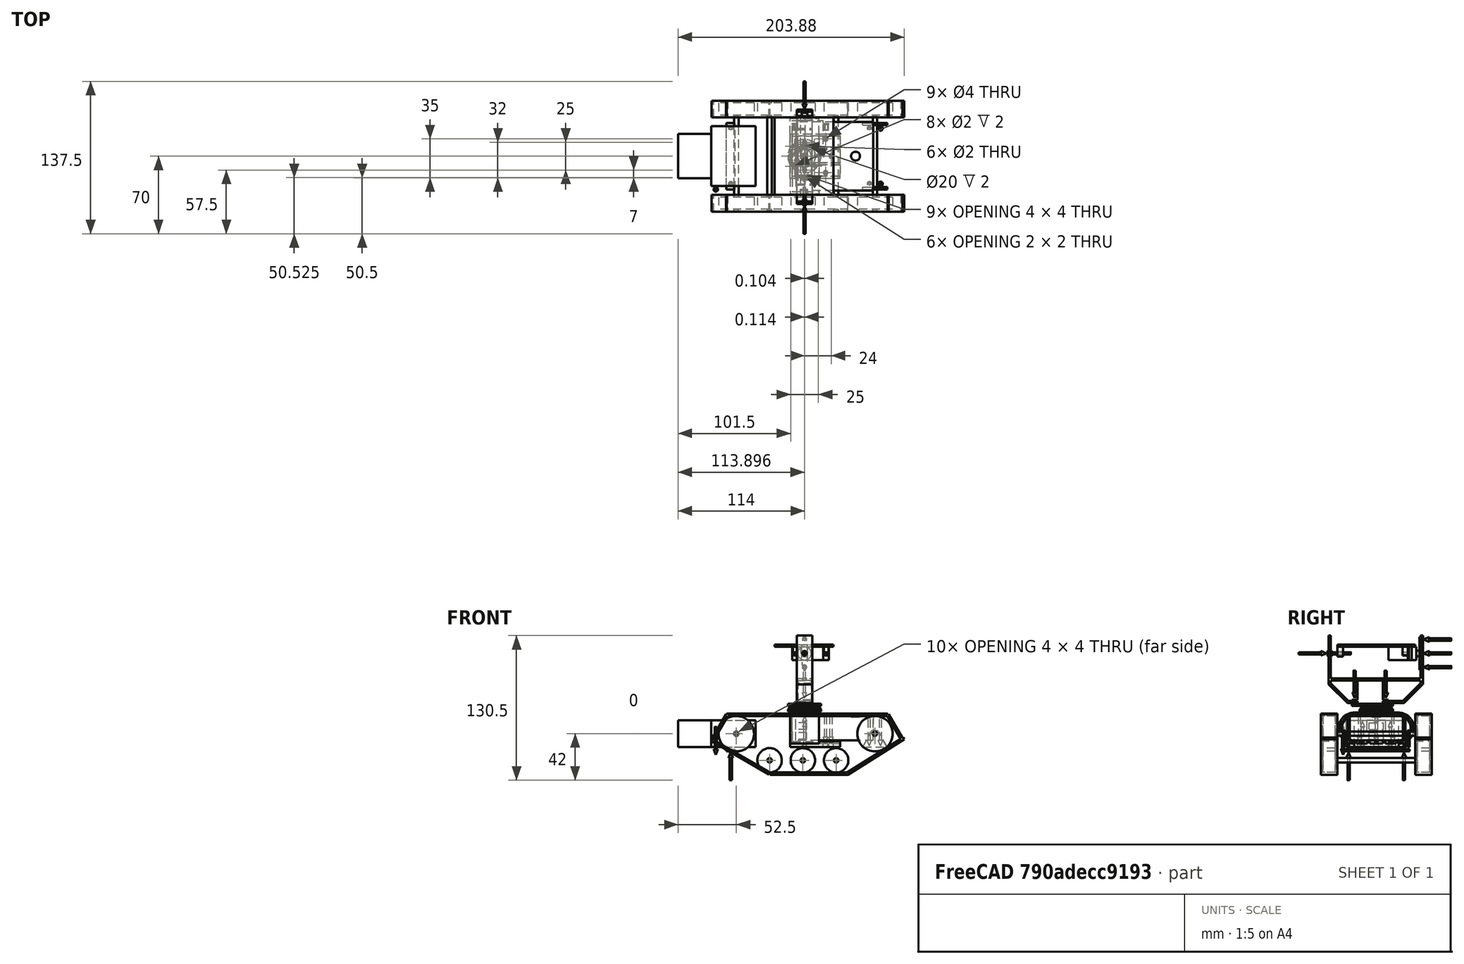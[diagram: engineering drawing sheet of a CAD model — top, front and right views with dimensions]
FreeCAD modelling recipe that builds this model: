
FCSTD DOCUMENT
Label: androidtank_10
License: CC-BY 3.0
LicenseURL: http://creativecommons.org/licenses/by/3.0/
objects: Part::Cylinder×59, Part::MultiFuse×47, Part::Box×40, Part::Cut×9, Part::Sphere×8, App::DocumentObjectGroup×3, Part::FeaturePython×1, Mesh::Feature×1, Part::Cone×1
note: 165 computed .brp shape members not serialized (recipe doc carries the construction recipe); baked Part::Feature solids carry a one-line shape summary decoded from their .brp

FEATURE [Part::Box] Box001001  label="Moter Unit2"
  Height = 24
  Length = 30
  Placement = pos=(-34,10,2) rot=(0,0,1;0rad)
  Width = 40
FEATURE [Part::Cylinder] Cylinder  label="Shaft"
  Angle = 360
  Height = 100
  Placement = pos=(20,-20,14) rot=(-1,0,0;1.5708rad)
  Radius = 2
FEATURE [Part::Box] Box001002
  Height = 2
  Length = 145
  Placement = pos=(10,-20,30) rot=(0,0,1;0rad)
  Width = 15
FEATURE [Part::Box] Box001002001
  Height = 2
  Length = 70
  Placement = pos=(49,-20,-23) rot=(0,0,1;0rad)
  Width = 15
FEATURE [Part::Box] Box001002001001
  Height = 2
  Length = 60
  Placement = pos=(119,-20,-23) rot=(0,-1,0;0.558505rad)
  Width = 15
FEATURE [Part::Box] Box001002001002
  Height = 2
  Length = 60
  Placement = pos=(49,-20,-21) rot=(0,1,0;3.66519rad)
  Width = 15
FEATURE [Part::Box] Box001002001003
  Height = 2
  Length = 26
  Placement = pos=(-2,-20,8) rot=(0,-1,0;1.0472rad)
  Width = 15
FEATURE [Part::Box] Box001002001003001
  Height = 2
  Length = 26
  Placement = pos=(169,-20,9) rot=(0,-1,0;2.0944rad)
  Width = 15
FEATURE [Part::MultiFuse] Fusion002001002  label="Caterpiller1"
  Shapes = -> [Box001002,Box001002001,Box001002001002,Box001002001001,Box001002001003,Box001002001003001]
FEATURE [Part::MultiFuse] Fusion002001002001  label="Caterpiller2"
  Placement = pos=(0,85,0) rot=(0,0,1;0rad)
  Shapes = -> [Box001002,Box001002001,Box001002001002,Box001002001001,Box001002001003,Box001002001003001]
FEATURE [Part::Cylinder] Cylinder002001001002  label="Wheel006"
  Angle = 360
  Height = 11
  Placement = pos=(20,78,14) rot=(1,0,0;1.5708rad)
  Radius = 11
FEATURE [Part::Cylinder] Cylinder002001001002001  label="Wheel007"
  Angle = 360
  Height = 11
  Placement = pos=(20,-7,14) rot=(1,0,0;1.5708rad)
  Radius = 11
FEATURE [Part::Cylinder] Cylinder002001002001  label="Shaft002"
  Angle = 360
  Height = 100
  Placement = pos=(20,-20,14) rot=(-1,0,0;1.5708rad)
  Radius = 2
FEATURE [Part::MultiFuse] Fusion002001002002002  label="SWheelSet1"
  Placement = pos=(28.5,0,-24) rot=(0,0,1;0rad)
  Shapes = -> [Cylinder002001002001,Cylinder002001001002,Cylinder002001001002001]
FEATURE [Part::MultiFuse] Fusion002001002002002001  label="SWheelSet2"
  Placement = pos=(58.5,0,-24) rot=(0,0,1;0rad)
  Shapes = -> [Cylinder002001002001,Cylinder002001001002,Cylinder002001001002001]
FEATURE [Part::MultiFuse] Fusion002001002002002001001  label="SWheelSet3"
  Placement = pos=(88.5,0,-24) rot=(0,0,1;0rad)
  Shapes = -> [Cylinder002001002001,Cylinder002001001002,Cylinder002001001002001]
FEATURE [Part::Box] Box001002001003002
  Height = 22
  Length = 70
  Placement = pos=(0,0,-11) rot=(0,0,1;0rad)
  Width = 40
FEATURE [Part::Cylinder] Cylinder002001001002002
  Angle = 360
  Height = 70
  Placement = pos=(0,0,0) rot=(0,1,0;1.5708rad)
  Radius = 11
FEATURE [Part::Cylinder] Cylinder001
  Angle = 360
  Height = 70
  Placement = pos=(0,40,0) rot=(0,1,0;1.5708rad)
  Radius = 11
FEATURE [Part::Cylinder] Cylinder002001001002003  label="PowerButton"
  Angle = 360
  Height = 2
  Placement = pos=(16,20,10) rot=(0,0,1;0rad)
  Radius = 4
FEATURE [Part::Box] Box001002001003003  label="USB1"
  Height = 6
  Length = 15
  Placement = pos=(60,13.5,-1) rot=(0,0,1;0rad)
  Width = 13
FEATURE [Part::Box] Box001001001  label="USB2"
  Height = 6
  Length = 15
  Placement = pos=(60,13.5,-10) rot=(0,0,1;0rad)
  Width = 13
FEATURE [Part::MultiFuse] Fusion002001002002002001002
  Shapes = -> [Cylinder001,Box001002001003002,Cylinder002001001002002]
FEATURE [Part::MultiFuse] Fusion001001
  Shapes = -> [Box001001001,Cylinder002001001002003,Box001002001003003]
FEATURE [Part::Cut] Cut  label="Eneloop"
  Base = -> Fusion002001002002002001002
  Placement = pos=(142,50,19) rot=(0,0,1;3.14159rad)
  Tool = -> Fusion001001
FEATURE [Part::Cylinder] Cylinder001001  label="Cylinder002"
  Angle = 360
  Height = 26
  Placement = pos=(0,50,19) rot=(0,1,0;1.5708rad)
  Radius = 14
FEATURE [Part::Box] Box001002001003002001  label="Box001002001003002001001001001006001001002001003001006001002"
  Height = 28
  Length = 26
  Placement = pos=(0,10,5) rot=(0,0,1;0rad)
  Width = 40
FEATURE [Part::Cylinder] Cylinder002001001002002001  label="Cylinder003"
  Angle = 360
  Height = 26
  Placement = pos=(0,10,19) rot=(0,1,0;1.5708rad)
  Radius = 14
FEATURE [Part::Box] Box001  label="Moter Unit1"
  Height = 24
  Length = 40
  Placement = pos=(-4,3,2) rot=(0,0,1;0rad)
  Width = 54
FEATURE [Part::Box] Box001002001003002001001  label="Box003"
  Height = 5
  Length = 45
  Placement = pos=(0,10,2) rot=(0,0,1;0rad)
  Width = 40
FEATURE [Part::Box] Box001002001003002001002  label="Box004"
  Height = 24
  Length = 26
  Placement = pos=(2,10,7) rot=(0,0,1;0rad)
  Width = 40
FEATURE [Part::Cylinder] Cylinder001001001  label="Cylinder004"
  Angle = 360
  Height = 26
  Placement = pos=(2,50,19) rot=(0,1,0;1.5708rad)
  Radius = 12
FEATURE [Part::Cylinder] Cylinder002001001002002001001  label="Cylinder005"
  Angle = 360
  Height = 26
  Placement = pos=(2,10,19) rot=(0,1,0;1.5708rad)
  Radius = 12
FEATURE [Part::Box] Box001002001003002001001001  label="Box006"
  Height = 3
  Length = 45
  Placement = pos=(2,12,5) rot=(0,0,1;0rad)
  Width = 10
FEATURE [Part::Box] Box001002001003002001001001001  label="Box007"
  Height = 3
  Length = 45
  Placement = pos=(2,24,5) rot=(0,0,1;0rad)
  Width = 12
FEATURE [Part::Box] Box001002001003002001001001001001  label="Box008"
  Height = 3
  Length = 45
  Placement = pos=(2,38,5) rot=(0,0,1;0rad)
  Width = 10
FEATURE [Part::MultiFuse] Fusion002001002002002001003
  Shapes = -> [Box001002001003002001,Cylinder001001,Cylinder002001001002002001,Box001002001003002001001]
FEATURE [Part::Cylinder] Cylinder002001001002002001002001  label="Cylinder007"
  Angle = 360
  Height = 40
  Placement = pos=(80,17.5,0) rot=(0,0,1;0rad)
  Radius = 1
FEATURE [Part::Cylinder] Cylinder002001001002002001002  label="Cylinder006"
  Angle = 360
  Height = 40
  Placement = pos=(80,42.5,0) rot=(0,0,1;0rad)
  Radius = 1
FEATURE [Part::Cylinder] Cylinder002001001002002001002001001  label="Cylinder008"
  Angle = 360
  Height = 40
  Placement = pos=(104,30,0) rot=(0,0,1;0rad)
  Radius = 2
FEATURE [Part::Cylinder] Cylinder002001001002002001002001002  label="Cylinder009"
  Angle = 360
  Height = 40
  Placement = pos=(99,45.5,0) rot=(0,0,1;0rad)
  Radius = 2
FEATURE [Part::Cylinder] Cylinder002001001002002001002001003  label="Cylinder0010"
  Angle = 360
  Height = 40
  Placement = pos=(99,15,0) rot=(0,0,1;0rad)
  Radius = 2
FEATURE [Part::Box] Box001002001003002001001001001006  label="Box009"
  Height = 2
  Length = 53
  Placement = pos=(47,-5,100) rot=(0,0,1;0rad)
  Width = 70
FEATURE [Part::Box] Box001002001003002001001001001006001  label="Box010"
  Height = 44
  Length = 14
  Placement = pos=(67,70,66) rot=(0,0,1;0rad)
  Width = 2
FEATURE [Part::Box] Box001002001003002001001001001006001001  label="Box011"
  Height = 2
  Length = 13
  Placement = pos=(67.5,12.5,48) rot=(0,0,1;0rad)
  Width = 23.5
FEATURE [Part::Box] Box001002001003002001001001001006001001001  label="Box012"
  Height = 44
  Length = 14
  Placement = pos=(67,-13,66) rot=(0,0,1;0rad)
  Width = 2
FEATURE [Part::Cylinder] Cylinder002001001002002001002001008  label="Hole1"
  Angle = 360
  Height = 20
  Placement = pos=(74,-20,94) rot=(-1,0,0;1.5708rad)
  Radius = 1.5
FEATURE [Part::Cylinder] Cylinder002001001002002001002001008001  label="Hole2"
  Angle = 360
  Height = 20
  Placement = pos=(74,60,106.5) rot=(-1,0,0;1.5708rad)
  Radius = 1
FEATURE [Part::Cylinder] Cylinder002001001002002001002001008001001  label="Hole4"
  Angle = 360
  Height = 20
  Placement = pos=(74,38.5,41) rot=(0,0,1;0rad)
  Radius = 1
FEATURE [Part::Cylinder] Cylinder002001001002002001002001008001001001  label="Hole3"
  Angle = 360
  Height = 20
  Placement = pos=(74,60,81.5) rot=(-1,0,0;1.5708rad)
  Radius = 1
FEATURE [Part::Cylinder] Cylinder002001001002002001002001008001001002  label="Hole5"
  Angle = 360
  Height = 20
  Placement = pos=(74,10.5,41) rot=(0,0,1;0rad)
  Radius = 1
FEATURE [Part::Box] Box001002001003002001001001001006001001001001  label="Box013"
  Height = 24
  Length = 14
  Placement = pos=(67,4,49) rot=(1,0,0;0.785397rad)
  Width = 2
FEATURE [Part::Box] Box001002001003002001001001001006001001001001001  label="Box014"
  Height = 24
  Length = 14
  Placement = pos=(67,53.41,50.41) rot=(-1,0,0;0.785397rad)
  Width = 2
FEATURE [Part::Box] Box001002001003002001001001001006001001002001  label="Box016"
  Height = 2
  Length = 14
  Placement = pos=(67,4,49) rot=(0,0,1;0rad)
  Width = 9
FEATURE [Part::Box] Box001002001003002001001001001006001001002001001  label="Box017"
  Height = 2
  Length = 14
  Placement = pos=(67,36,49) rot=(0,0,1;0rad)
  Width = 19
FEATURE [Part::Box] Box001002001003002001001001001006001001002001002  label="Box015"
  Height = 2
  Length = 14
  Placement = pos=(67,-13,69.5) rot=(0,0,1;0rad)
  Width = 85
FEATURE [Part::MultiFuse] Fusion002001002002002001009
  Shapes = -> [Box001002001003002001001001001006001,Box001002001003002001001001001006001001001001,Box001002001003002001001001001006001001001,Box001002001003002001001001001006001001001001001,Box001002001003002001001001001006001001002001,Box001002001003002001001001001006001001002001002,Box001002001003002001001001001006001001002001001]
FEATURE [Part::Cylinder] Cylinder002001001002002001002001008001001002001  label="Hole006"
  Angle = 360
  Height = 20
  Placement = pos=(74,10.5,60) rot=(0,0,1;0rad)
  Radius = 2
FEATURE [Part::Cylinder] Cylinder002001001002002001002001008001001002002  label="Hole007"
  Angle = 360
  Height = 20
  Placement = pos=(74,38.5,60) rot=(0,0,1;0rad)
  Radius = 2
FEATURE [Part::MultiFuse] Fusion002001002002002001010
  Shapes = -> [Cylinder002001001002002001002001008001,Box001002001003002001001001001006001001,Cylinder002001001002002001002001008001001,Cylinder002001001002002001002001008,Cylinder002001001002002001002001008001001001,Cylinder002001001002002001002001008001001002,Cylinder002001001002002001002001008001001002002,Cylinder002001001002002001002001008001001002001]
FEATURE [Part::Cut] Cut003  label="HeadFrame"
  Base = -> Fusion002001002002002001009
  Placement = pos=(6,0,-7.5) rot=(0,0,1;0rad)
  Tool = -> Fusion002001002002002001010
FEATURE [Part::Cylinder] Cylinder002001001002002001002001008001001002003  label="Cylinder025"
  Angle = 360
  Height = 5
  Placement = pos=(74,0,94) rot=(1,0,0;1.5708rad)
  Radius = 3
FEATURE [Part::Box] Box001002001003002001001001001006001001002001003  label="Box020"
  Height = 6
  Length = 6
  Placement = pos=(71,-5,94) rot=(0,0,1;0rad)
  Width = 5
FEATURE [Part::Cylinder] Cylinder002001001002002001002001008001001002003001  label="Cylinder026"
  Angle = 360
  Height = 7
  Placement = pos=(74,1,94) rot=(1,0,0;1.5708rad)
  Radius = 1.5
FEATURE [Part::Box] Box001002001003002001001001001006001001002001003001001  label="Box022"
  Height = 6
  Length = 4
  Placement = pos=(91.5,53.5,94) rot=(0,0,1;0rad)
  Width = 5
FEATURE [Part::Cylinder] Cylinder002001001002002001002001008001001002003002  label="Cylinder027"
  Angle = 360
  Height = 5
  Placement = pos=(65.5,58.5,94) rot=(1,0,0;1.5708rad)
  Radius = 2
FEATURE [Part::Cylinder] Cylinder002001001002002001002001008001001002003002001  label="Cylinder028"
  Angle = 360
  Height = 5
  Placement = pos=(93.5,58.5,94) rot=(1,0,0;1.5708rad)
  Radius = 2
FEATURE [Part::Box] Box001002001003002001001001001006001001002001003001  label="Box021"
  Height = 6
  Length = 4
  Placement = pos=(63.5,53.5,94) rot=(0,0,1;0rad)
  Width = 5
FEATURE [Part::Cylinder] Cylinder002001001002002001002001008001001002003002002  label="Cylinder029"
  Angle = 360
  Height = 6
  Placement = pos=(65.5,59,94) rot=(1,0,0;1.5708rad)
  Radius = 1
FEATURE [Part::Cylinder] Cylinder002001001002002001002001008001001002003002001001  label="Cylinder030"
  Angle = 360
  Height = 6
  Placement = pos=(93.5,59,94) rot=(1,0,0;1.5708rad)
  Radius = 1
FEATURE [Part::MultiFuse] Fusion002001002002002001011
  Shapes = -> [Box001002001003002001001001001006,Box001002001003002001001001001006001001002001003001001,Cylinder002001001002002001002001008001001002003002001,Box001002001003002001001001001006001001002001003,Cylinder002001001002002001002001008001001002003,Box001002001003002001001001001006001001002001003001,Cylinder002001001002002001002001008001001002003002]
FEATURE [Part::MultiFuse] Fusion002001002002002001012
  Shapes = -> [Cylinder002001001002002001002001008001001002003001,Cylinder002001001002002001002001008001001002003002002,Cylinder002001001002002001002001008001001002003002001001]
FEATURE [Part::Cut] Cut002003  label="HeadMount"
  Base = -> Fusion002001002002002001011
  Placement = pos=(6,0,-7.5) rot=(0,0,1;0rad)
  Tool = -> Fusion002001002002002001012
FEATURE [Part::Cylinder] Cylinder002001001002002001002001001001  label="Cylinder040"
  Angle = 360
  Height = 40
  Placement = pos=(80,30,0) rot=(0,0,1;0rad)
  Radius = 2
FEATURE [Part::Box] Box001002001003002001001001001006001001002001003001002  label="ServoBody"
  Height = 21
  Length = 23
  Width = 12
FEATURE [Part::Cylinder] Cylinder002001001002002001002001008001001002003002001002  label="ServoBody2"
  Angle = 360
  Height = 4
  Placement = pos=(6,6,21) rot=(0,0,1;0rad)
  Radius = 6
FEATURE [Part::Box] Box001002001003002001001001001006001001002001003001003  label="ServoBody3"
  Height = 1
  Length = 33
  Placement = pos=(-5,0,17.5) rot=(0,0,1;0rad)
  Width = 12
FEATURE [Part::Cylinder] Cylinder001001002  label="ServoAxis"
  Angle = 360
  Height = 4
  Placement = pos=(6,6,24) rot=(0,0,1;0rad)
  Radius = 2.5
FEATURE [Part::MultiFuse] Fusion005  label="ServoArmL"
  Shapes = -> [Cylinder001001002,Box001002001003002001001001001006001001002001003001003,Box001002001003002001001001001006001001002001003001002,Cylinder002001001002002001002001008001001002003002001002]
FEATURE [Part::MultiFuse] Fusion006  label="ServoYaw"
  Placement = pos=(86,36,62) rot=(0.707107,-0.707107,0;3.14159rad)
  Shapes = -> [Fusion005]
FEATURE [Part::Cylinder] Cylinder003001001004  label="Cylinder002001001002002001002001008001001002003002001006"
  Angle = 360
  Height = 0.5
  Placement = pos=(-2.5,6,20.5) rot=(0,0,1;0rad)
  Radius = 2
FEATURE [Part::Cylinder] Cylinder003001001005  label="Cylinder011"
  Angle = 360
  Height = 2
  Placement = pos=(6,6,21) rot=(0,0,1;0rad)
  Radius = 15
FEATURE [Part::Cylinder] Cylinder003001001004001  label="Cylinder010"
  Angle = 360
  Height = 0.5
  Placement = pos=(25.5,6,20.5) rot=(0,0,1;0rad)
  Radius = 2
FEATURE [Part::Cylinder] Cylinder003001001005001  label="Cylinder012"
  Angle = 360
  Height = 2
  Placement = pos=(6,6,21) rot=(0,0,1;0rad)
  Radius = 6.5
FEATURE [Part::Cylinder] Cylinder003001001005001001  label="Cylinder013"
  Angle = 360
  Height = 2
  Placement = pos=(12,6,21) rot=(0,0,1;0rad)
  Radius = 3.5
FEATURE [Part::Box] Box002
  Height = 2
  Length = 10
  Placement = pos=(18,3,21) rot=(0,0,1;0rad)
  Width = 6
FEATURE [Part::Cylinder] Cylinder003001001004002  label="Cylinder014"
  Angle = 360
  Height = 5
  Placement = pos=(-2.5,6,19.5) rot=(0,0,1;0rad)
  Radius = 1
FEATURE [Part::Cylinder] Cylinder003001001004001001  label="Cylinder015"
  Angle = 360
  Height = 5
  Placement = pos=(25.5,6,19.5) rot=(0,0,1;0rad)
  Radius = 1
FEATURE [Part::MultiFuse] Fusion008
  Shapes = -> [Cylinder003001001005,Box002,Cylinder003001001004,Cylinder003001001004001]
FEATURE [Part::MultiFuse] Fusion009
  Shapes = -> [Cylinder003001001005001,Cylinder003001001005001001,Cylinder003001001004002,Cylinder003001001004001001]
FEATURE [Part::Cut] Cut002  label="Guide1"
  Base = -> Fusion008
  Placement = pos=(86,36,62) rot=(-0.705662,0.708549,0;3.14159rad)
  Tool = -> Fusion009
FEATURE [Part::Box] Box001002001003002001001001001006001001002001003001004  label="ServoBody004"
  Height = 21
  Length = 23
  Width = 12
FEATURE [Part::Cylinder] Cylinder002001001002002001002001008001001002003002001003  label="ServoBody005"
  Angle = 360
  Height = 4
  Placement = pos=(6,6,21) rot=(0,0,1;0rad)
  Radius = 6
FEATURE [Part::Box] Box001002001003002001001001001006001001002001003001005  label="ServoBody006"
  Height = 1
  Length = 33
  Placement = pos=(-5,0,17.5) rot=(0,0,1;0rad)
  Width = 12
FEATURE [Part::Cylinder] Cylinder001001003  label="ServoAxis001"
  Angle = 360
  Height = 4
  Placement = pos=(6,6,24) rot=(0,0,1;0rad)
  Radius = 2.5
FEATURE [Part::MultiFuse] Fusion005001  label="ServoArmL001"
  Shapes = -> [Cylinder001001003,Box001002001003002001001001001006001001002001003001005,Box001002001003002001001001001006001001002001003001004,Cylinder002001001002002001002001008001001002003002001003]
FEATURE [Part::Cylinder] Cylinder002001001002002001002001008001001002003002001004  label="Cylinder002001001002002001002001008001001002003002001012"
  Angle = 360
  Height = 2
  Radius = 2.5
FEATURE [Part::FeaturePython] Scale  # Draft clone (typed FeaturePython)
  Objects = -> [Cylinder002001001002002001002001008001001002003002001004]
  Placement = pos=(0,0,1) rot=(0,0,1;0rad)
  Scale = (6,1,0.5)
FEATURE [Part::MultiFuse] Fusion  label="Arm"
  Placement = pos=(6,6,27) rot=(0,0,1;1.5708rad)
  Shapes = -> [Cylinder002001001002002001002001008001001002003002001004,Scale]
FEATURE [Part::MultiFuse] Fusion006001  label="ServoPitch"
  Placement = pos=(74,41,92.5) rot=(-1,0,0;1.5708rad)
  Shapes = -> [Fusion005001,Fusion]
FEATURE [Part::Cylinder] Cylinder002001001002002001002001008001001002003002001005  label="Wheel1"
  Angle = 360
  Height = 11
  Placement = pos=(20,78,14) rot=(1,0,0;1.5708rad)
  Radius = 16
FEATURE [Part::Cylinder] Cylinder002001001002002001002001008001001002003002001005001  label="Wheel2"
  Angle = 360
  Height = 11
  Placement = pos=(20,-7,14) rot=(1,0,0;1.5708rad)
  Radius = 16
FEATURE [Part::MultiFuse] Fusion002001002002002001014  label="LWheelSet1"
  Placement = pos=(-1.5,0,0) rot=(0,0,1;0rad)
  Shapes = -> [Cylinder,Cylinder002001001002002001002001008001001002003002001005,Cylinder002001001002002001002001008001001002003002001005001]
FEATURE [Part::MultiFuse] Fusion002001002002002001014001  label="LWheelSet2"
  Placement = pos=(123.5,0,0) rot=(0,0,1;0rad)
  Shapes = -> [Cylinder,Cylinder002001001002002001002001008001001002003002001005,Cylinder002001001002002001002001008001001002003002001005001]
FEATURE [Part::Cylinder] Cylinder003001001003  label="Cylinder002001001002002001002001008001001002003002001013"
  Angle = 360
  Height = 2
  Placement = pos=(6,6,26) rot=(0,0,1;0rad)
  Radius = 15
FEATURE [Part::Sphere] Sphere
  Angle1 = -90
  Angle2 = 0
  Angle3 = 360
  Placement = pos=(-3,-3,26) rot=(0,0,1;0rad)
  Radius = 2
FEATURE [Part::Sphere] Sphere001
  Angle1 = -90
  Angle2 = 0
  Angle3 = 360
  Placement = pos=(15,-3,26) rot=(0,0,1;0rad)
  Radius = 2
FEATURE [Part::Sphere] Sphere001001  label="Sphere002"
  Angle1 = -90
  Angle2 = 0
  Angle3 = 360
  Placement = pos=(15,15,26) rot=(0,0,1;0rad)
  Radius = 2
FEATURE [Part::Sphere] Sphere001001001  label="Sphere003"
  Angle1 = -90
  Angle2 = 0
  Angle3 = 360
  Placement = pos=(-3,15,26) rot=(0,0,1;0rad)
  Radius = 2
FEATURE [Part::Cylinder] Cylinder003001001005001004  label="Cylinder020"
  Angle = 360
  Height = 4
  Placement = pos=(-6.5,6,26) rot=(0,0,1;0rad)
  Radius = 1
FEATURE [Part::Cylinder] Cylinder003001001001003  label="Cylinder021"
  Angle = 360
  Height = 4
  Placement = pos=(18.5,6,26) rot=(0,0,1;0rad)
  Radius = 1
FEATURE [Part::Cylinder] Cylinder003001001005001003001  label="Cylinder022"
  Angle = 360
  Height = 5
  Placement = pos=(-3,-3,26) rot=(0,0,1;0rad)
  Radius = 1
FEATURE [Part::Cylinder] Cylinder003001001001002001  label="Cylinder023"
  Angle = 360
  Height = 5
  Placement = pos=(15,-3,26) rot=(0,0,1;0rad)
  Radius = 1
FEATURE [Part::Sphere] Sphere001001001001  label="Sphere004"
  Angle1 = -90
  Angle2 = 0
  Angle3 = 360
  Placement = pos=(-6.5,6,26) rot=(0,0,1;0rad)
  Radius = 2
FEATURE [Part::Sphere] Sphere001001001001001  label="Sphere005"
  Angle1 = -90
  Angle2 = 0
  Angle3 = 360
  Placement = pos=(18.5,6,26) rot=(0,0,1;0rad)
  Radius = 2
FEATURE [Part::Sphere] Sphere001001001001001001  label="Sphere006"
  Angle1 = -90
  Angle2 = 0
  Angle3 = 360
  Placement = pos=(6,-6.5,26) rot=(0,0,1;0rad)
  Radius = 2
FEATURE [Part::Sphere] Sphere001001001001001001001  label="Sphere007"
  Angle1 = -90
  Angle2 = 0
  Angle3 = 360
  Placement = pos=(6,18.5,26) rot=(0,0,1;0rad)
  Radius = 2
FEATURE [Part::Cylinder] Cylinder003001001003001  label="Cylinder024"
  Angle = 360
  Height = 2
  Placement = pos=(6,6,26) rot=(0,0,1;0rad)
  Radius = 10
FEATURE [Part::MultiFuse] Fusion014
  Shapes = -> [Sphere,Cylinder003001001003,Sphere001001001,Sphere001001001001001001,Sphere001001001001,Sphere001,Sphere001001,Sphere001001001001001001001,Sphere001001001001001]
FEATURE [Part::Cylinder] Cylinder003001001005001003001001  label="Cylinder002001001002002001002001008001001002003002001014"
  Angle = 360
  Height = 5
  Placement = pos=(-3,15,26) rot=(0,0,1;0rad)
  Radius = 1
FEATURE [Part::Cylinder] Cylinder003001001001002001001  label="Cylinder002001001002002001002001008001001002003002001015"
  Angle = 360
  Height = 5
  Placement = pos=(15,15,26) rot=(0,0,1;0rad)
  Radius = 1
FEATURE [Part::Cylinder] Cylinder003001001005001003001001001  label="Cylinder002001001002002001002001008001001002003002001016"
  Angle = 360
  Height = 5
  Placement = pos=(6,18.5,26) rot=(0,0,1;0rad)
  Radius = 1
FEATURE [Part::Cylinder] Cylinder003001001005001003001001001001  label="Cylinder002001001002002001002001008001001002003002001017"
  Angle = 360
  Height = 5
  Placement = pos=(6,-6.5,26) rot=(0,0,1;0rad)
  Radius = 1
FEATURE [Part::MultiFuse] Fusion015
  Shapes = -> [Cylinder003001001003001,Cylinder003001001005001004,Cylinder003001001001003,Cylinder003001001005001003001,Cylinder003001001001002001,Cylinder003001001005001003001001,Cylinder003001001005001003001001001001,Cylinder003001001001002001001,Cylinder003001001005001003001001001]
FEATURE [Part::Cut] Cut002005  label="Guide2"
  Base = -> Fusion014
  Placement = pos=(74,36,62) rot=(1,0,0;3.14159rad)
  Tool = -> Fusion015
FEATURE [Part::MultiFuse] Fusion002001002002002001014002
  Shapes = -> [Box001002001003002001002,Cylinder001001001,Cylinder002001001002002001001,Box001002001003002001001001,Box001002001003002001001001001,Box001002001003002001001001001001]
FEATURE [Part::Cut] Cut002006
  Base = -> Fusion002001002002002001003
  Placement = pos=(67,0,0) rot=(0,0,1;0rad)
  Tool = -> Fusion002001002002002001014002
FEATURE [Part::Cylinder] Cylinder002001001002002001002001001001001  label="Cylinder041"
  Angle = 360
  Height = 20
  Placement = pos=(80,42.5,0) rot=(0,0,1;0rad)
  Radius = 2
FEATURE [Part::Cylinder] Cylinder002001001002002001002001001001001001  label="Cylinder042"
  Angle = 360
  Height = 20
  Placement = pos=(80,17.5,0) rot=(0,0,1;0rad)
  Radius = 2
FEATURE [Part::Box] Box001002001003003001  label="USB003"
  Height = 10
  Length = 15
  Placement = pos=(60,21.5,16) rot=(0,0,1;0rad)
  Width = 17
FEATURE [Part::MultiFuse] Fusion002001002002002001014003
  Shapes = -> [Cylinder002001001002002001002001,Cylinder002001001002002001002,Cylinder002001001002002001002001001,Cylinder002001001002002001002001002,Cylinder002001001002002001002001003,Cylinder002001001002002001002001001001,Cylinder002001001002002001002001001001001,Box001002001003003001,Cylinder002001001002002001002001001001001001]
FEATURE [Part::Cut] Cut002007  label="BatteryFrame2"
  Base = -> Cut002006
  Tool = -> Fusion002001002002002001014003
FEATURE [Part::Box] Box001002001003002001001001001006001001002001003001006  label="Box040"
  Height = 15
  Length = 22
  Placement = pos=(0,0,2) rot=(0,0,1;0rad)
  Width = 2
FEATURE [Part::Box] Box001002001003002001001001001006001001002001003001006001  label="Box041"
  Height = 20
  Length = 10
  Placement = pos=(22,0,2) rot=(0,-1,0;0.523599rad)
  Width = 2
FEATURE [Part::Box] Box001002001003002001001001001006001001002001003001006001001  label="Box042"
  Height = 20
  Length = 10
  Placement = pos=(-8.71,0,7) rot=(0,1,0;0.523599rad)
  Width = 2
FEATURE [Part::MultiFuse] Fusion002001002002002001014004
  Shapes = -> [Box001002001003002001001001001006001001002001003001006001001,Box001002001003002001001001001006001001002001003001006001]
FEATURE [Part::Cut] Cut002008  label="LWheelMount1"
  Base = -> Box001002001003002001001001001006001001002001003001006
  Placement = pos=(132.5,0,0) rot=(0,0,1;0rad)
  Tool = -> Fusion002001002002002001014004
FEATURE [Part::Cut] Cut002008001  label="LWheelMount2"
  Base = -> Box001002001003002001001001001006001001002001003001006
  Placement = pos=(132.5,58,0) rot=(0,0,1;0rad)
  Tool = -> Fusion002001002002002001014004
FEATURE [Mesh::Feature] UniversalPlate
FEATURE [Part::Box] Box  label="MotorMount"
  Height = 2
  Length = 8
  Placement = pos=(9.5,0,-2) rot=(0,0,1;0rad)
  Width = 60
FEATURE [App::DocumentObjectGroup] ____________  label="DriveFrame"
  Group = -> [Box001,Box001001,Fusion002001002,Fusion002001002001,Fusion002001002002002,Fusion002001002002002001,Fusion002001002002002001001,Fusion002001002002002001014,Fusion002001002002002001014001,Cut002008,Cut002008001,UniversalPlate,Box]
FEATURE [Part::Cone] Cone
  Angle = 360
  Height = 5
  Placement = pos=(0,0,-5) rot=(0,0,1;0rad)
  Radius1 = 0
  Radius2 = 2
FEATURE [Part::Cylinder] Cylinder002001001002002001002001008001001002003002001005002
  Angle = 360
  Height = 20
  Radius = 1
FEATURE [Part::MultiFuse] Fusion002001002002002001014005  label="ArrowOrig"
  Shapes = -> [Cone,Cylinder002001001002002001002001008001001002003002001005002]
FEATURE [Part::MultiFuse] Fusion002001002002002001014005001  label="Arrow001"
  Placement = pos=(148.5,5,8) rot=(0,0,1;0rad)
  Shapes = -> [Cone,Cylinder002001001002002001002001008001001002003002001005002]
FEATURE [Part::MultiFuse] Fusion002001002002002001014005001001  label="Arrow002"
  Placement = pos=(138.5,5,8) rot=(0,0,1;0rad)
  Shapes = -> [Cone,Cylinder002001001002002001002001008001001002003002001005002]
FEATURE [Part::MultiFuse] Fusion002001002002002001014005001002  label="Arrow003"
  Placement = pos=(148.5,55,8) rot=(0,0,1;0rad)
  Shapes = -> [Cone,Cylinder002001001002002001002001008001001002003002001005002]
FEATURE [Part::MultiFuse] Fusion002001002002002001014005001002001  label="Arrow004"
  Placement = pos=(138.5,55,8) rot=(0,0,1;0rad)
  Shapes = -> [Cone,Cylinder002001001002002001002001008001001002003002001005002]
FEATURE [Part::MultiFuse] Fusion002001002002002001014005001002002  label="Arrow005"
  Placement = pos=(13.5,5,-8) rot=(1,0,0;3.14159rad)
  Shapes = -> [Cone,Cylinder002001001002002001002001008001001002003002001005002]
FEATURE [Part::MultiFuse] Fusion002001002002002001014005001002002001  label="Arrow006"
  Placement = pos=(13.5,55,-8) rot=(1,0,0;3.14159rad)
  Shapes = -> [Cone,Cylinder002001001002002001002001008001001002003002001005002]
FEATURE [Part::MultiFuse] Fusion002001002002002001014005001002002002  label="Arrow007"
  Placement = pos=(80,17.5,20) rot=(1,0,0;3.14159rad)
  Shapes = -> [Cone,Cylinder002001001002002001002001008001001002003002001005002]
FEATURE [Part::MultiFuse] Fusion002001002002002001014005001002002002001  label="Arrow008"
  Placement = pos=(80,42.5,20) rot=(1,0,0;3.14159rad)
  Shapes = -> [Cone,Cylinder002001001002002001002001008001001002003002001005002]
FEATURE [Part::MultiFuse] Fusion002001002002002001014005001002002002002  label="Arrow009"
  Placement = pos=(80,10.5,51) rot=(0,0,1;0rad)
  Shapes = -> [Cone,Cylinder002001001002002001002001008001001002003002001005002]
FEATURE [Part::MultiFuse] Fusion002001002002002001014005001002002002003  label="Arrow010"
  Placement = pos=(80,38.5,51) rot=(0,0,1;0rad)
  Shapes = -> [Cone,Cylinder002001001002002001002001008001001002003002001005002]
FEATURE [Part::MultiFuse] Fusion002001002002002001014005001002002002002001  label="Arrow011"
  Placement = pos=(80,77.5,86.5) rot=(-1,0,0;1.5708rad)
  Shapes = -> [Cone,Cylinder002001001002002001002001008001001002003002001005002]
FEATURE [Part::MultiFuse] Fusion002001002002002001014005001002002002002001001  label="Arrow012"
  Placement = pos=(80,77.5,99) rot=(-1,0,0;1.5708rad)
  Shapes = -> [Cone,Cylinder002001001002002001002001008001001002003002001005002]
FEATURE [Part::MultiFuse] Fusion002001002002002001014005001002002002002001001001  label="Arrow013"
  Placement = pos=(80,77.5,74) rot=(-1,0,0;1.5708rad)
  Shapes = -> [Cone,Cylinder002001001002002001002001008001001002003002001005002]
FEATURE [Part::MultiFuse] Fusion002001002002002001014005001002002002002001001002  label="Arrow014"
  Placement = pos=(80,-20,86.5) rot=(1,0,0;1.5708rad)
  Shapes = -> [Cone,Cylinder002001001002002001002001008001001002003002001005002]
FEATURE [Part::MultiFuse] Fusion002001002002002001014005001002002002002001001003  label="Arrow015"
  Placement = pos=(80,30,25) rot=(1,0,0;3.14159rad)
  Shapes = -> [Cone,Cylinder002001001002002001002001008001001002003002001005002]
FEATURE [Part::MultiFuse] Fusion002001002002002001014005001002002002002001001004  label="Arrow016"
  Placement = pos=(104,30,11) rot=(0,0,1;0rad)
  Shapes = -> [Cone,Cylinder002001001002002001002001008001001002003002001005002]
FEATURE [Part::MultiFuse] Fusion002001002002002001014005001002002002002001001004001  label="Arrow017"
  Placement = pos=(99,45,11) rot=(0,0,1;0rad)
  Shapes = -> [Cone,Cylinder002001001002002001002001008001001002003002001005002]
FEATURE [Part::MultiFuse] Fusion002001002002002001014005001002002002002001001004001001  label="Arrow018"
  Placement = pos=(99,15,11) rot=(0,0,1;0rad)
  Shapes = -> [Cone,Cylinder002001001002002001002001008001001002003002001005002]
FEATURE [App::DocumentObjectGroup] ____________001  label="Arrows"
  Group = -> [Fusion002001002002002001014005,Fusion002001002002002001014005001,Fusion002001002002002001014005001001,Fusion002001002002002001014005001002,Fusion002001002002002001014005001002001,Fusion002001002002002001014005001002002,Fusion002001002002002001014005001002002001,Fusion002001002002002001014005001002002002,Fusion002001002002002001014005001002002002001,Fusion002001002002002001014005001002002002002,+9 more]
FEATURE [Part::MultiFuse] Fusion002001002002002001014005001002002002002001001004001002  label="Arm001"
  Placement = pos=(80,30,35) rot=(0.707107,0.707107,0;3.14159rad)
  Shapes = -> [Cylinder002001001002002001002001008001001002003002001004,Scale]
FEATURE [Part::Cylinder] Cylinder002001001002002001002001008001001002003002001005003
  Angle = 360
  Height = 1
  Placement = pos=(0,0,-1) rot=(0,0,1;0rad)
  Radius = 2
FEATURE [Part::Cylinder] Cylinder002001001002002001002001008001001002003002001005003001
  Angle = 360
  Height = 20
  Radius = 1
FEATURE [Part::MultiFuse] Fusion002001002002002001014005001002002002002001001004001003  label="Vise"
  Placement = pos=(80,-13,86.5) rot=(-1,0,0;1.5708rad)
  Shapes = -> [Cylinder002001001002002001002001008001001002003002001005003,Cylinder002001001002002001002001008001001002003002001005003001]
FEATURE [Part::Box] Box001002001003002001001001001006001001002001003001006001002  label="Nat"
  Height = 5
  Length = 5
  Placement = pos=(77.5,-11,84) rot=(0,0,1;0rad)
  Width = 1
FEATURE [App::DocumentObjectGroup] ____________002  label="Guide"
  Group = -> [Fusion002001002002002001014005001002002002002001001004001002,Fusion002001002002002001014005001002002002002001001004001003,Box001002001003002001001001001006001001002001003001006001002]
